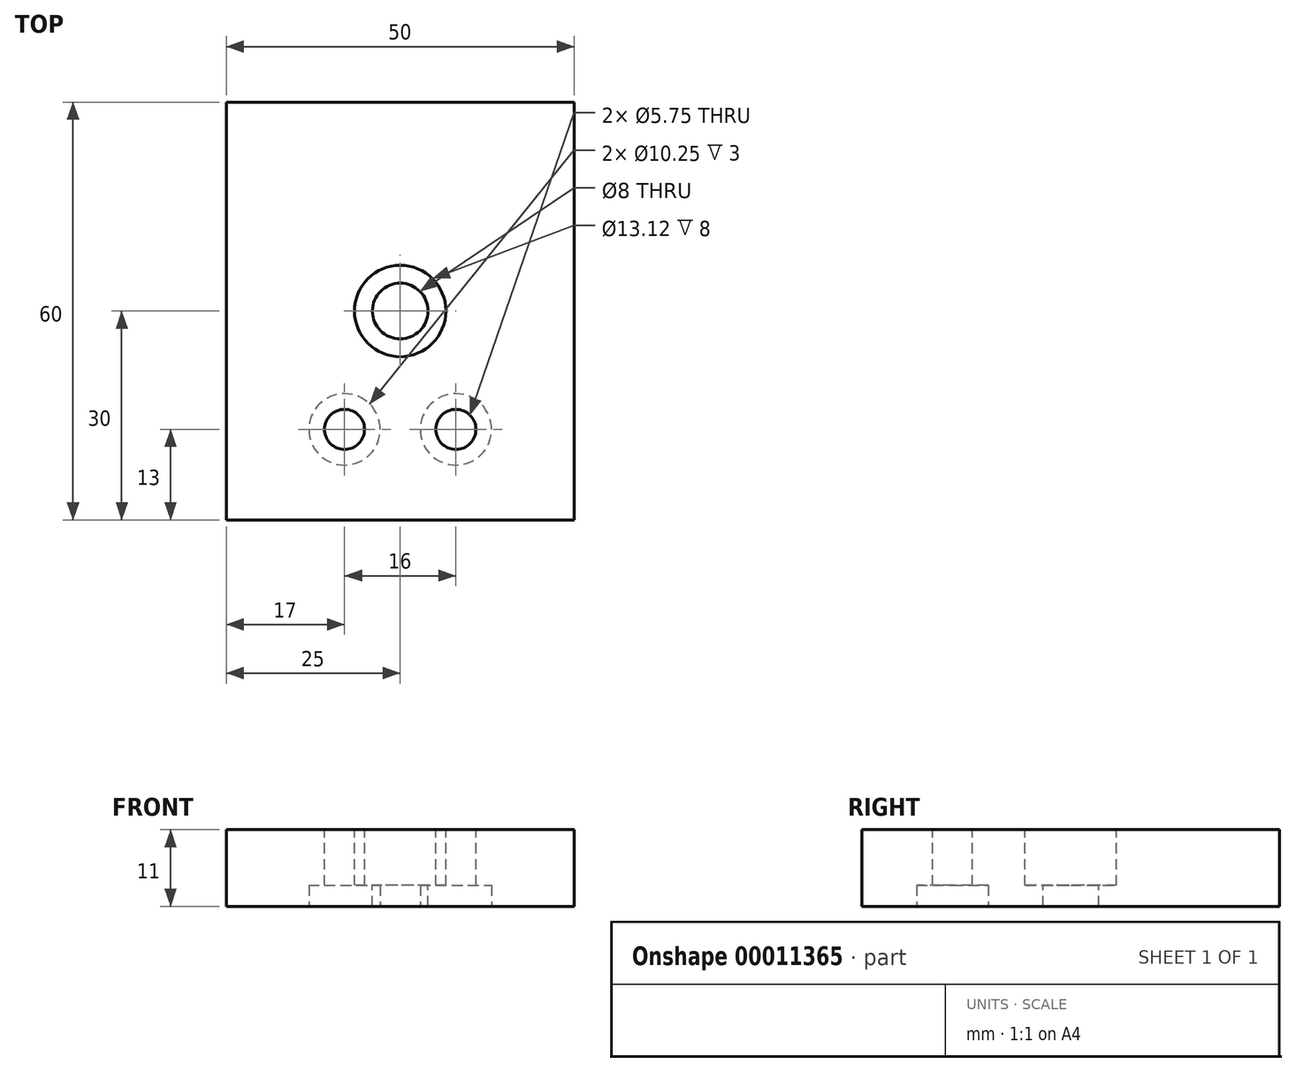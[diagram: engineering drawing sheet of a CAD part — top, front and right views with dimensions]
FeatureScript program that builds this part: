
annotation { "Feature Type Name" : "Feature", "Feature Type Description" : "" }
export const myFeature = defineFeature(function(context is Context, id is Id, definition is map)
    precondition{}
    {
        {
            var Q0;
            Q0=qCreatedBy(makeId("Top.planeOp"),FACE);
            var sketch = newSketch(context, id + "F0", { "sketchPlane" : qUnion([Q0])});
            skLineSegment(sketch, "E0.bottom", {"start": v(-25, 30) * mm, "end": v(25, 30) * mm});
            skLineSegment(sketch, "E0.top", {"start": v(-25, -30) * mm, "end": v(25, -30) * mm});
            skLineSegment(sketch, "E0.left", {"start": v(-25, 30) * mm, "end": v(-25, -30) * mm});
            skLineSegment(sketch, "E0.right", {"start": v(25, 30) * mm, "end": v(25, -30) * mm});
            skSolve(sketch);
        }
        {
            var Q0;
            Q0=makeQuery(id+"F0.imprint","IMPRINT",FACE,{"disambiguationData":[TD([[makeQuery(id+"F0.imprint","IMPRINT",EDGE,{"derivedFrom":sQuery(id+"F0.wireOp",EDGE,"E0.bottom")}),-1.0]])]});
            extrude(context, id + "F1", {"entities" : qUnion([Q0]), "depth" : 11 * mm});
        }
        {
            var Q0;
            Q0=makeQuery(id+"F1.opExtrude","CAP_FACE",FACE,{"disambiguationData":[OSD([sQuery(id+"F0.wireOp",EDGE,"E0.bottom"),sQuery(id+"F0.wireOp",EDGE,"E0.top"),sQuery(id+"F0.wireOp",EDGE,"E0.left"),sQuery(id+"F0.wireOp",EDGE,"E0.right")])],"isStart":false});
            var sketch = newSketch(context, id + "F2", { "sketchPlane" : qUnion([Q0])});
            skCircle(sketch, "E1", {"center": v(0, 0) * mm, "radius": 4 * mm});
            skCircle(sketch, "E2", {"center": v(-8, -17) * mm, "radius": 2.88 * mm});
            skCircle(sketch, "E3.0.MirrorC", {"center": v(8, -17) * mm, "radius": 2.88 * mm});
            skSolve(sketch);
        }
        {
            var Q0;
            Q0=qSketchRegion(id+"F2",true);
            var Q1;
            Q1=makeQuery(id+"F1.opExtrude","CAP_FACE",FACE,{"disambiguationData":[OSD([sQuery(id+"F0.wireOp",EDGE,"E0.bottom"),sQuery(id+"F0.wireOp",EDGE,"E0.top"),sQuery(id+"F0.wireOp",EDGE,"E0.left"),sQuery(id+"F0.wireOp",EDGE,"E0.right")])],"isStart":true});
            extrude(context, id + "F3", {"entities" : qUnion([Q0]), "operationType" : NewBodyOperationType.REMOVE, "endBound" : BoundingType.UP_TO_SURFACE, "oppositeDirection" : true, "endBoundEntityFace" : qUnion([Q1]), "depth" : 25 * mm});
        }
        {
            var Q0;
            Q0=makeQuery(id+"F1.opExtrude","CAP_FACE",FACE,{"disambiguationData":[OSD([sQuery(id+"F0.wireOp",EDGE,"E0.bottom"),sQuery(id+"F0.wireOp",EDGE,"E0.top"),sQuery(id+"F0.wireOp",EDGE,"E0.left"),sQuery(id+"F0.wireOp",EDGE,"E0.right")])],"isStart":false});
            var sketch = newSketch(context, id + "F4", { "sketchPlane" : qUnion([Q0])});
            skCircle(sketch, "E4", {"center": v(0, 0) * mm, "radius": 6.56 * mm});
            skSolve(sketch);
        }
        {
            var Q0;
            Q0=qSketchRegion(id+"F4",true);
            extrude(context, id + "F5", {"entities" : qUnion([Q0]), "operationType" : NewBodyOperationType.REMOVE, "oppositeDirection" : true, "depth" : 8 * mm});
        }
        {
            var Q0;
            Q0=makeQuery(id+"F1.opExtrude","CAP_FACE",FACE,{"disambiguationData":[OSD([sQuery(id+"F0.wireOp",EDGE,"E0.bottom"),sQuery(id+"F0.wireOp",EDGE,"E0.top"),sQuery(id+"F0.wireOp",EDGE,"E0.left"),sQuery(id+"F0.wireOp",EDGE,"E0.right")])],"isStart":true});
            var sketch = newSketch(context, id + "F6", { "sketchPlane" : qUnion([Q0])});
            skCircle(sketch, "E5", {"center": v(-8, 17) * mm, "radius": 5.12 * mm});
            skCircle(sketch, "E6.0.MirrorC", {"center": v(8, 17) * mm, "radius": 5.12 * mm});
            skSolve(sketch);
        }
        {
            var Q0;
            Q0=qSketchRegion(id+"F6",true);
            extrude(context, id + "F7", {"entities" : qUnion([Q0]), "operationType" : NewBodyOperationType.REMOVE, "oppositeDirection" : true, "depth" : 3 * mm});
        }
    });
